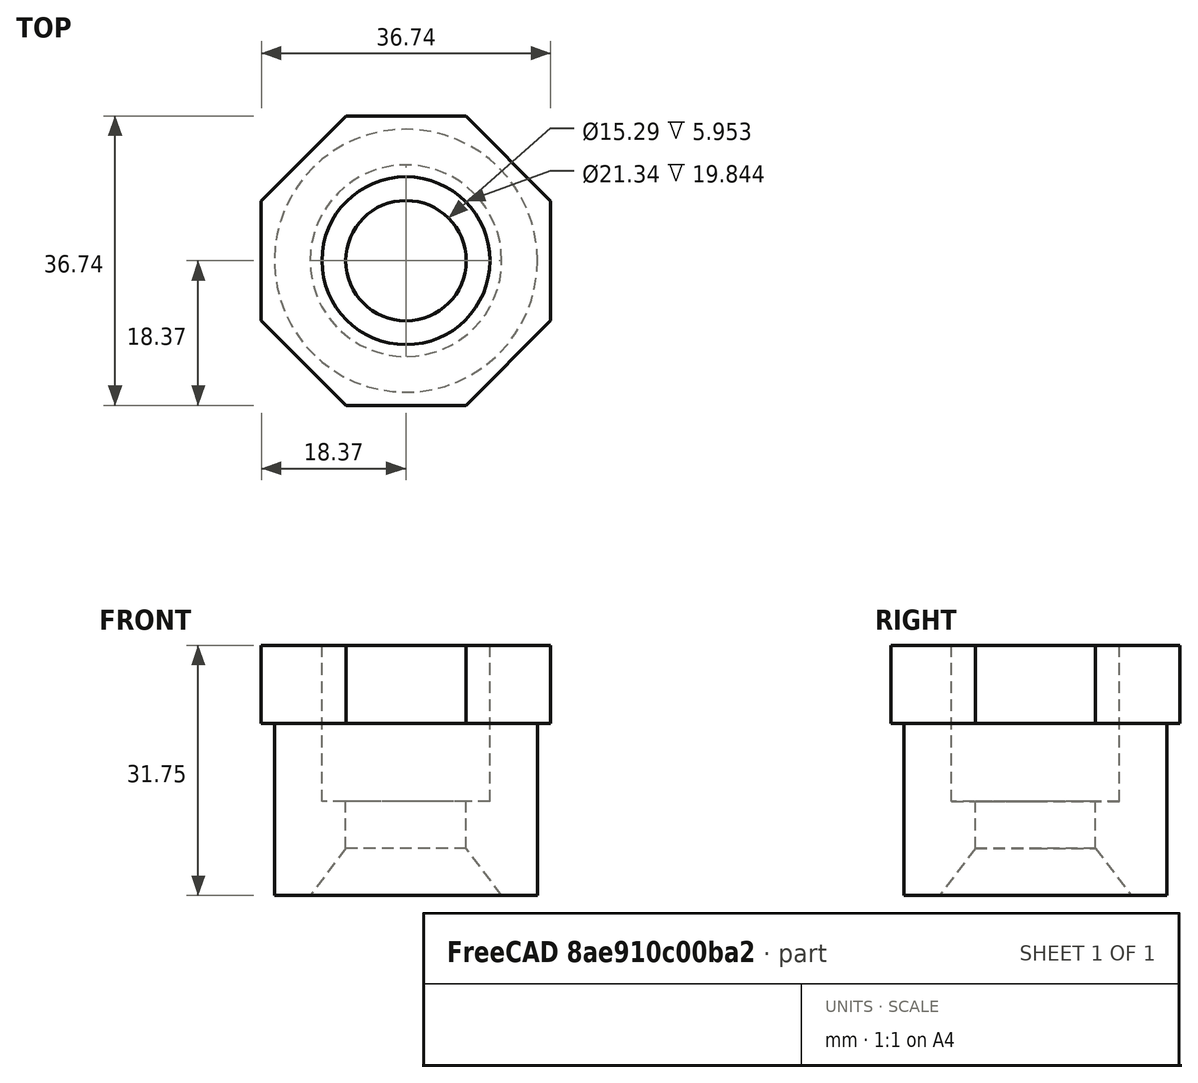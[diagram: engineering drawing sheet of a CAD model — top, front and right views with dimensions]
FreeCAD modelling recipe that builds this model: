
FCSTD DOCUMENT  (FreeCAD 0.17R13303 (Git))
Label: bushing-test
License: All rights reserved
LicenseURL: http://en.wikipedia.org/wiki/All_rights_reserved
objects: Part::Cylinder×3, Part::Box×2, Part::MultiFuse×2, Part::MultiCommon×1, Part::Cone×1, Part::Cut×1
note: 10 computed .brp shape members not serialized (recipe doc carries the construction recipe); baked Part::Feature solids carry a one-line shape summary decoded from their .brp

FEATURE [Part::Cylinder] OuterCynlider
  Angle = 360
  AttacherType = Attacher::AttachEngine3D
  Height = 31.75
  Radius = 16.7005
FEATURE [Part::Box] Box
  AttacherType = Attacher::AttachEngine3D
  Height = 9.92188
  Length = 36.7411
  Placement = pos=(-18.3706,-18.3706,0) rot=(0,0,1;0rad)
  Width = 36.7411
FEATURE [Part::Box] Box001
  AttacherType = Attacher::AttachEngine3D
  Height = 9.92188
  Length = 36.7411
  Placement = pos=(0,-25.9799,0) rot=(0,0,1;0.785398rad)
  Width = 36.7411
FEATURE [Part::MultiCommon] Common
  Placement = pos=(0,0,21.8281) rot=(0,0,1;0rad)
  Shapes = -> [Box,Box001]
FEATURE [Part::MultiFuse] Fusion
  Shapes = -> [OuterCynlider,Common]
FEATURE [Part::Cylinder] OuterCynlider001
  Angle = 360
  AttacherType = Attacher::AttachEngine3D
  Height = 31.75
  Radius = 7.6454
FEATURE [Part::Cylinder] OuterCynlider002
  Angle = 360
  AttacherType = Attacher::AttachEngine3D
  Height = 19.8438
  Placement = pos=(0,0,11.9062) rot=(0,0,1;0rad)
  Radius = 10.668
FEATURE [Part::Cone] Cone
  Angle = 360
  AttacherType = Attacher::AttachEngine3D
  Height = 5.95312
  Radius1 = 12.173
  Radius2 = 7.6454
FEATURE [Part::MultiFuse] Fusion001
  Shapes = -> [OuterCynlider001,OuterCynlider002,Cone]
FEATURE [Part::Cut] Cut  label="437-130"
  Base = -> Fusion
  Tool = -> Fusion001
